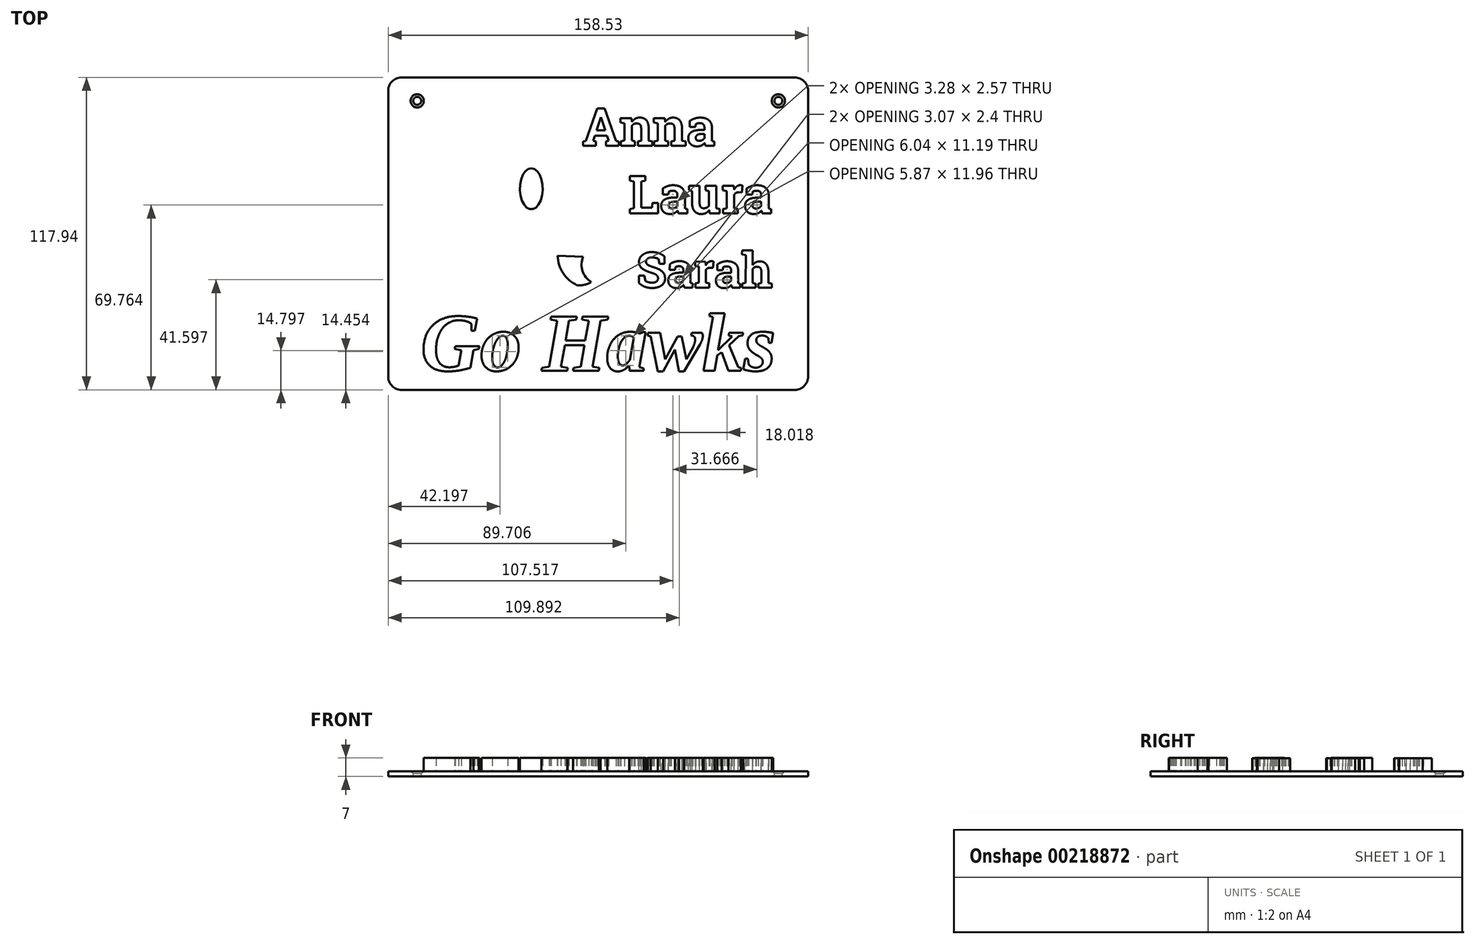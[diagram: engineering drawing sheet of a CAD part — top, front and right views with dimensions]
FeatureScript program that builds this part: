
annotation { "Feature Type Name" : "Feature", "Feature Type Description" : "" }
export const myFeature = defineFeature(function(context is Context, id is Id, definition is map)
    precondition{}
    {
        {
            var Q0;
            Q0=qCreatedBy(makeId("Top.planeOp"),FACE);
            var sketch = newSketch(context, id + "F0", { "sketchPlane" : qUnion([Q0])});
            skArc(sketch, "E0", {"start": v(-57.55, 8.32) * mm, "mid": v(-30.54, 33.34) * mm, "end": v(2.03, 16.18) * mm});
            skArc(sketch, "E1", {"start": v(2.03, 16.18) * mm, "mid": v(1.32, 7.42) * mm, "end": v(-7.44, 8.14) * mm});
            skArc(sketch, "E2", {"start": v(-57.55, 8.32) * mm, "mid": v(-53.9, 12.01) * mm, "end": v(-48.96, 13.6) * mm});
            skArc(sketch, "E3", {"start": v(-48.96, 13.6) * mm, "mid": v(-54.18, 8.71) * mm, "end": v(-56.94, 2.1) * mm});
            skArc(sketch, "E4", {"start": v(-56.94, 2.1) * mm, "mid": v(-54.22, 4.43) * mm, "end": v(-50.82, 5.54) * mm});
            skArc(sketch, "E5", {"start": v(-50.82, 5.54) * mm, "mid": v(-54.53, 0.52) * mm, "end": v(-56.34, -5.44) * mm});
            skArc(sketch, "E6", {"start": v(-56.34, -5.44) * mm, "mid": v(-53.94, -2.78) * mm, "end": v(-50.62, -1.41) * mm});
            skArc(sketch, "E7", {"start": v(-50.62, -1.41) * mm, "mid": v(-54.3, -7.87) * mm, "end": v(-52.79, -15.15) * mm});
            skArc(sketch, "E8", {"start": v(-52.79, -15.15) * mm, "mid": v(-40.6, 1.18) * mm, "end": v(-23.59, 12.4) * mm});
            skEllipse(sketch, "E9", {"center": v(-19.56, 9.63) * mm, "majorRadius": 7.74 * mm, "minorRadius": 4.31 * mm, "majorAxis": v(0, 1)});
            skArc(sketch, "E10", {"start": v(-7.44, 8.14) * mm, "mid": v(-11.16, 10.22) * mm, "end": v(-15.33, 11.16) * mm});
            skSolve(sketch);
        }
        {
            var Q0;
            Q0=qCreatedBy(makeId("Top.planeOp"),FACE);
            var sketch = newSketch(context, id + "F1", { "sketchPlane" : qUnion([Q0])});
            skArc(sketch, "E11", {"start": v(-8.57, -10.45) * mm, "mid": v(-2.72, -0.6) * mm, "end": v(5.1, 7.77) * mm});
            skArc(sketch, "E12", {"start": v(5.1, 7.77) * mm, "mid": v(11.24, -7.66) * mm, "end": v(9.48, -24.17) * mm});
            skArc(sketch, "E13", {"start": v(-8.57, -10.45) * mm, "mid": v(3.49, -13.32) * mm, "end": v(9.48, -24.17) * mm});
            skSolve(sketch);
        }
        {
            var Q0;
            Q0=qCreatedBy(makeId("Top.planeOp"),FACE);
            var sketch = newSketch(context, id + "F2", { "sketchPlane" : qUnion([Q0])});
            skArc(sketch, "E14", {"start": v(-9.6, -15.7) * mm, "mid": v(-7.54, -22.32) * mm, "end": v(-2.27, -26.8) * mm});
            skArc(sketch, "E15", {"start": v(-2.27, -26.8) * mm, "mid": v(0.52, -26.67) * mm, "end": v(3.1, -25.59) * mm});
            skArc(sketch, "E16", {"start": v(3.1, -25.59) * mm, "mid": v(-0.23, -21.44) * mm, "end": v(0, -16.13) * mm});
            skLineSegment(sketch, "E17", {"start": v(-9.6, -15.7) * mm, "end": v(0, -16.13) * mm});
            skSolve(sketch);
        }
        {
            var Q0;
            Q0=qCreatedBy(makeId("Top.planeOp"),FACE);
            var sketch = newSketch(context, id + "F3", { "sketchPlane" : qUnion([Q0])});
            skArc(sketch, "E18", {"start": v(-34.23, 2.41) * mm, "mid": v(-28.62, 0.68) * mm, "end": v(-29.52, -5.12) * mm});
            skArc(sketch, "E19", {"start": v(-29.52, -5.12) * mm, "mid": v(-31.93, -23.74) * mm, "end": v(-13.86, -18.67) * mm});
            skLineSegment(sketch, "E20", {"start": v(-13.86, -18.67) * mm, "end": v(-13.04, 0) * mm});
            skArc(sketch, "E21", {"start": v(-34.23, 2.41) * mm, "mid": v(-30.84, 5.04) * mm, "end": v(-26.98, 6.94) * mm});
            skArc(sketch, "E22", {"start": v(-26.98, 6.94) * mm, "mid": v(-21.9, -0.33) * mm, "end": v(-13.04, 0) * mm});
            skSolve(sketch);
        }
        {
            var Q0;
            Q0=makeQuery(id+"F0.imprint","IMPRINT",FACE,{"disambiguationData":[TD([[makeQuery(id+"F0.imprint","IMPRINT",EDGE,{"derivedFrom":sQuery(id+"F0.wireOp",EDGE,"E0")}),-1.0]])]});
            var Q1;
            {var subQ0=sQuery(id+"F0.wireOp",EDGE,"E9");var subQ1=makeQuery(id+"F0.imprint","INTERSECT",VERTEX,{"derivedFrom":[sQuery(id+"F0.wireOp",EDGE,"E8"),subQ0]});Q1=makeQuery(id+"F0.imprint","IMPRINT",FACE,{"disambiguationData":[TD([[makeQuery(id+"F0.imprint","IMPRINT",EDGE,{"disambiguationData":[TD([[subQ1,-1.0]])],"derivedFrom":subQ0}),1.0]])]});}
            var Q2;
            Q2=makeQuery(id+"F3.imprint","IMPRINT",FACE,{"disambiguationData":[TD([[makeQuery(id+"F3.imprint","IMPRINT",EDGE,{"derivedFrom":sQuery(id+"F3.wireOp",EDGE,"E18")}),1.0]])]});
            var Q3;
            Q3=makeQuery(id+"F1.imprint","IMPRINT",FACE,{"disambiguationData":[TD([[makeQuery(id+"F1.imprint","IMPRINT",EDGE,{"derivedFrom":sQuery(id+"F1.wireOp",EDGE,"E11")}),-1.0]])]});
            var Q4;
            Q4=makeQuery(id+"F2.imprint","IMPRINT",FACE,{"disambiguationData":[TD([[makeQuery(id+"F2.imprint","IMPRINT",EDGE,{"derivedFrom":sQuery(id+"F2.wireOp",EDGE,"E14")}),1.0]])]});
            extrude(context, id + "F4", {"entities" : qUnion([Q0, Q1, Q2, Q3, Q4]), "depth" : 5 * mm});
        }
        {
            var Q0;
            Q0=qCreatedBy(makeId("Top.planeOp"),FACE);
            var sketch = newSketch(context, id + "F5", { "sketchPlane" : qUnion([Q0])});
            skText(sketch, "E23", { "text": "Anna", "fontName": "RobotoSlab-Bold.ttf"});
            skText(sketch, "E24", { "text": "Sarah", "fontName": "RobotoSlab-Bold.ttf"});
            skText(sketch, "E25", { "text": "Laura", "fontName": "RobotoSlab-Bold.ttf"});
            const initialGuessF5  = {"E23": [-0.00042, 0.02584, 1, -0.0007, 0.01427], "E24": [0.0202, -0.02766, 1, -0.00267, 0.01337], "E25": [0.01712, 0.00026, 1, -0.00013, 0.0143]};
            skSetInitialGuess(sketch, initialGuessF5);
            skSolve(sketch);
        }
        {
            var Q0;
            Q0 = qSketchRegion(id + "F5", true);
            extrude(context, id + "F6", {"entities" : qUnion([Q0]), "depth" : 4.9 * mm});
        }
        {
            var Q0;
            Q0=qCreatedBy(makeId("Top.planeOp"),FACE);
            var sketch = newSketch(context, id + "F7", { "sketchPlane" : qUnion([Q0])});
            skText(sketch, "E26", { "text": "Go Hawks", "fontName": "Tinos-BoldItalic.ttf"});
            const initialGuessF7  = {"E26": [-0.06132, -0.05906, 1, 0, 0.02242]};
            skSetInitialGuess(sketch, initialGuessF7);
            skSolve(sketch);
        }
        {
            var Q0;
            Q0 = qSketchRegion(id + "F7", true);
            extrude(context, id + "F8", {"entities" : qUnion([Q0]), "depth" : 5 * mm});
        }
        {
            var Q0;
            Q0=qCreatedBy(makeId("Top.planeOp"),FACE);
            var sketch = newSketch(context, id + "F9", { "sketchPlane" : qUnion([Q0])});
            skLineSegment(sketch, "E27.bottom", {"start": v(-73.58, 51.6) * mm, "end": v(84.95, 51.6) * mm});
            skLineSegment(sketch, "E27.top", {"start": v(-73.58, -66.33) * mm, "end": v(84.95, -66.33) * mm});
            skLineSegment(sketch, "E27.left", {"start": v(-73.58, 51.6) * mm, "end": v(-73.58, -66.33) * mm});
            skLineSegment(sketch, "E27.right", {"start": v(84.95, 51.6) * mm, "end": v(84.95, -66.33) * mm});
            skPoint(sketch, "E27.middle", {"position": v(5.69, -7.36) * mm});
            skSolve(sketch);
        }
        {
            var Q0;
            Q0=makeQuery(id+"F9.imprint","IMPRINT",FACE,{"disambiguationData":[TD([[makeQuery(id+"F9.imprint","IMPRINT",EDGE,{"derivedFrom":sQuery(id+"F9.wireOp",EDGE,"E27.bottom")}),-1.0]])]});
            extrude(context, id + "F10", {"entities" : qUnion([Q0]), "oppositeDirection" : true, "depth" : 2 * mm});
        }
        {
            var Q0;
            Q0=makeQuery(id+"F10.opExtrude","SWEPT_EDGE",EDGE,{"disambiguationData":[OSD([sQuery(id+"F9.wireOp",EDGE,"E27.bottom"),sQuery(id+"F9.wireOp",EDGE,"E27.left")])]});
            var Q1;
            Q1=makeQuery(id+"F10.opExtrude","SWEPT_EDGE",EDGE,{"disambiguationData":[OSD([sQuery(id+"F9.wireOp",EDGE,"E27.bottom"),sQuery(id+"F9.wireOp",EDGE,"E27.right")])]});
            var Q2;
            Q2=makeQuery(id+"F10.opExtrude","SWEPT_EDGE",EDGE,{"disambiguationData":[OSD([sQuery(id+"F9.wireOp",EDGE,"E27.top"),sQuery(id+"F9.wireOp",EDGE,"E27.right")])]});
            var Q3;
            Q3=makeQuery(id+"F10.opExtrude","SWEPT_EDGE",EDGE,{"disambiguationData":[OSD([sQuery(id+"F9.wireOp",EDGE,"E27.top"),sQuery(id+"F9.wireOp",EDGE,"E27.left")])]});
            fillet(context, id + "F11", {"entities" : qUnion([Q0, Q1, Q2, Q3]), "radius" : 5 * mm, "tangentPropagation" : true, "allowEdgeOverflow" : false});
        }
        {
            var Q0;
            Q0=makeQuery(id+"F10.opExtrude","CAP_FACE",FACE,{"disambiguationData":[OSD([sQuery(id+"F9.wireOp",EDGE,"E27.bottom"),sQuery(id+"F9.wireOp",EDGE,"E27.top"),sQuery(id+"F9.wireOp",EDGE,"E27.left"),sQuery(id+"F9.wireOp",EDGE,"E27.right")])],"isStart":true});
            var sketch = newSketch(context, id + "F12", { "sketchPlane" : qUnion([Q0])});
            skPoint(sketch, "E28", {"position": v(-62.63, 42.81) * mm});
            skPoint(sketch, "E29", {"position": v(73.73, 42.81) * mm});
            skSolve(sketch);
        }
        {
            var Q0;
            Q0=sQuery(id+"F12.wireOp",VERTEX,"E28");
            var Q1;
            Q1=sQuery(id+"F12.wireOp",VERTEX,"E29");
            var Q2;
            Q2=makeQuery(id+"F10.opExtrude","SWEPT_BODY",BODY,{"disambiguationData":[OSD([sQuery(id+"F9.wireOp",EDGE,"E27.bottom"),sQuery(id+"F9.wireOp",EDGE,"E27.top"),sQuery(id+"F9.wireOp",EDGE,"E27.left"),sQuery(id+"F9.wireOp",EDGE,"E27.right")])]});
            hole(context, id + "F13", {"style" : HoleStyle.C_SINK, "endStyle" : HoleEndStyle.BLIND, "holeDiameter" : 3 * mm, "cSinkDiameter" : 5 * mm, "cSinkAngle" : 90 * degree, "holeDepth" : 4 * mm, "locations" : qUnion([Q0, Q1]), "scope" : qUnion([Q2])});
        }
    });
